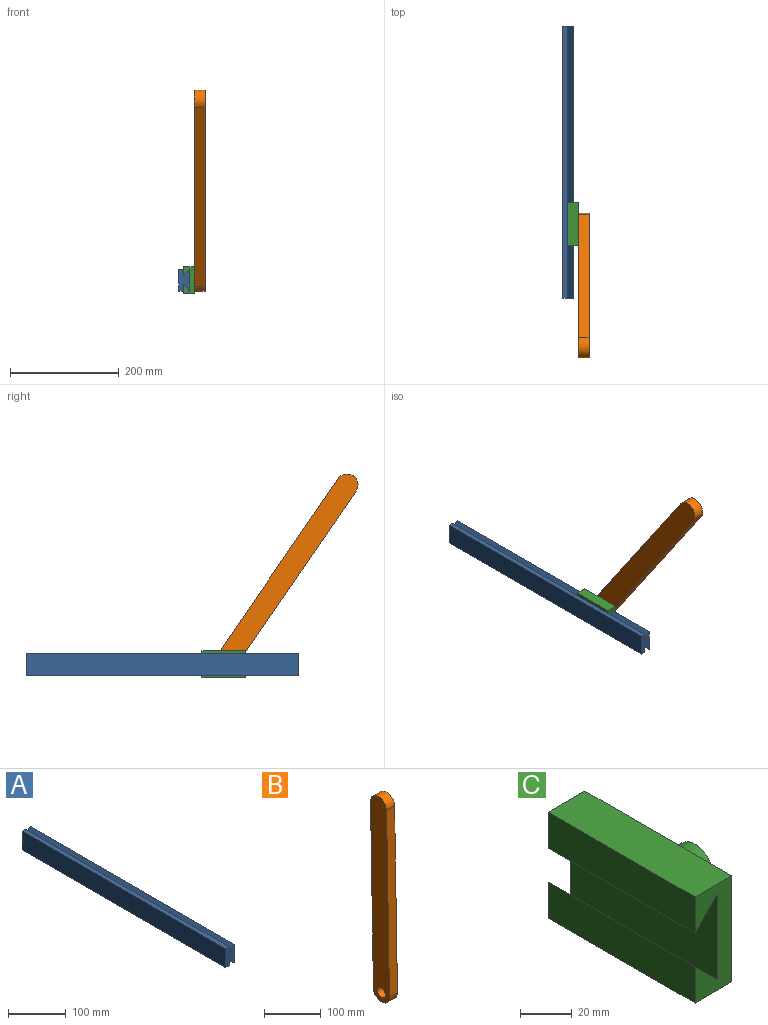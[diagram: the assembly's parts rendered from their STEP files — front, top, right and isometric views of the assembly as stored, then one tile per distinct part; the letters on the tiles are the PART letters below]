
ASSEMBLY  parts=3 mates=2
PART A: 10 faces, bbox 20x500x40 mm
  f0: plane 500x40mm, normal (1,0,0), area 20000mm2, adj f1,f5,f6,f7
  f1: plane 500x12mm, normal (-0.71,0,0.71), area 8485.3mm2, adj f0,f2,f5,f6
  f2: plane 500x12mm, normal (1,0,0), area 6000mm2, adj f1,f3,f5,f6
  f3: plane 500x8mm, normal (0,0,1), area 4000mm2, adj f2,f4,f5,f6
  f4: plane 500x40mm, normal (-1,0,0), area 20000mm2, adj f3,f5,f6,f9
  f5: plane 40x20mm, normal (0,-1,0), area 656mm2, adj f0,f1,f2,f3,f4,f7,f8,f9
  f6: plane 40x20mm, normal (0,1,0), area 656mm2, adj f0,f1,f2,f3,f4,f7,f8,f9
  f7: plane 500x12mm, normal (-0.71,0,-0.71), area 8485.3mm2, adj f0,f5,f6,f8
  f8: plane 500x12mm, normal (1,0,0), area 6000mm2, adj f5,f6,f7,f9
  f9: plane 500x8mm, normal (0,0,-1), area 4000mm2, adj f4,f5,f6,f8
PART B: 7 faces, bbox 20x47.2x439.9 mm
  f0: plane 399.94x20mm, normal (0,-1,0.02), area 8000mm2, adj f1,f3,f5,f6
  f1: cylinder r=20mm len=40mm, axis (-1,0,0), area 1256.6mm2, adj f0,f2,f5,f6
  f2: plane 399.94x20mm, normal (0,1,-0.02), area 8000mm2, adj f1,f3,f5,f6
  f3: cylinder r=20mm len=40mm, axis (-1,0,0), area 1256.6mm2, adj f0,f2,f5,f6
  f4: cylinder r=10mm len=20mm, axis (-1,0,0), area 1256.6mm2, adj f5,f6
  f5: plane 439.94x47.2mm, normal (1,0,0), area 16942.5mm2, adj f0,f1,f2,f3,f4
  f6: plane 439.94x47.2mm, normal (-1,0,0), area 16942.5mm2, adj f0,f1,f2,f3,f4
PART C: 12 faces, bbox 40x80x50 mm
  f0: plane 80x17mm, normal (-1,0,0), area 1360mm2, adj f1,f7,f8,f9
  f1: plane 80x20mm, normal (0,0,1), area 1600mm2, adj f0,f2,f8,f9
  f2: plane 80x50mm, normal (1,0,0), area 3685.8mm2, adj f1,f3,f8,f9,f10
  f3: plane 80x20mm, normal (0,0,-1), area 1600mm2, adj f2,f4,f8,f9
  f4: plane 80x17mm, normal (-1,0,0), area 1360mm2, adj f3,f5,f8,f9
  f5: plane 80x12mm, normal (0.71,0,0.71), area 1357.6mm2, adj f4,f6,f8,f9
  f6: plane 80x40mm, normal (-1,0,0), area 3200mm2, adj f5,f7,f8,f9
  f7: plane 80x12mm, normal (0.71,0,-0.71), area 1357.6mm2, adj f0,f6,f8,f9
  f8: plane 50x20mm, normal (0,1,0), area 664mm2, adj f0,f1,f2,f3,f4,f5,f6,f7
  f9: plane 50x20mm, normal (0,-1,0), area 664mm2, adj f0,f1,f2,f3,f4,f5,f6,f7
  f10: cylinder r=10mm len=20mm, axis (-1,0,0), area 1256.6mm2, adj f2,f11
  f11: plane 20x20mm, normal (1,0,0), area 314.2mm2, adj f10
PLACE A t=(-175.21,80.63,-93.66)mm fixed
PLACE B rot(axis=(1,0,0),35.5deg) t=(-174.8,-315.21,-116.91)mm
PLACE C t=(-174.8,-322.66,-93.66)mm
MATE revolute C.f10 <-> B.f4  axis (1,0,0) through (-166.8,-282.66,-93.66)mm
MATE slider C.f9 <-> A.f5  axis (0,-1,0) through (-175.21,-322.66,-93.66)mm
